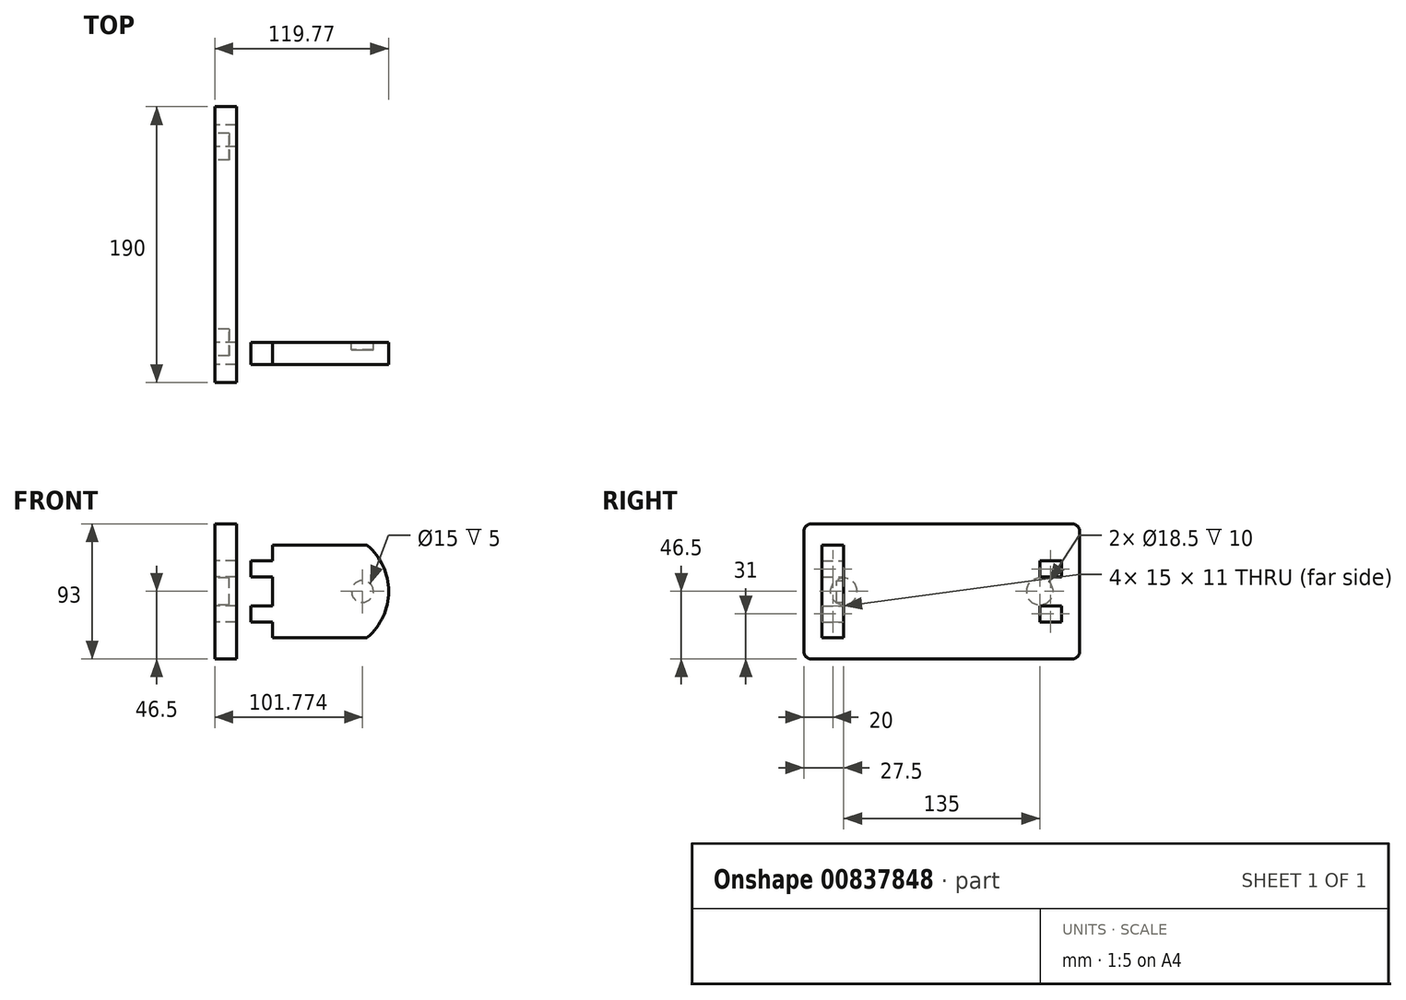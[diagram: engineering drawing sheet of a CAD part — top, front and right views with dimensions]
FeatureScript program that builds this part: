
annotation { "Feature Type Name" : "Feature", "Feature Type Description" : "" }
export const myFeature = defineFeature(function(context is Context, id is Id, definition is map)
    precondition{}
    {
        {
            var Q0;
            Q0=qCreatedBy(makeId("Right.planeOp"),FACE);
            var sketch = newSketch(context, id + "F0", { "sketchPlane" : qUnion([Q0])});
            skLineSegment(sketch, "E0.bottom", {"start": v(90, -46.5) * mm, "end": v(-90, -46.5) * mm});
            skLineSegment(sketch, "E0.top", {"start": v(90, 46.5) * mm, "end": v(-90, 46.5) * mm});
            skLineSegment(sketch, "E0.left", {"start": v(95, -41.5) * mm, "end": v(95, 41.5) * mm});
            skLineSegment(sketch, "E0.right", {"start": v(-95, -41.5) * mm, "end": v(-95, 41.5) * mm});
            skPoint(sketch, "E0.middle", {"position": v(0, 0) * mm});
            skLineSegment(sketch, "E1.bottom", {"start": v(67.5, 21) * mm, "end": v(82.5, 21) * mm});
            skLineSegment(sketch, "E1.top", {"start": v(67.5, 10) * mm, "end": v(82.5, 10) * mm});
            skLineSegment(sketch, "E1.left", {"start": v(67.5, 21) * mm, "end": v(67.5, 10) * mm});
            skLineSegment(sketch, "E1.right", {"start": v(82.5, 21) * mm, "end": v(82.5, 10) * mm});
            skLineSegment(sketch, "E2.bottom", {"start": v(67.5, -10) * mm, "end": v(82.5, -10) * mm});
            skLineSegment(sketch, "E2.top", {"start": v(67.5, -21) * mm, "end": v(82.5, -21) * mm});
            skLineSegment(sketch, "E2.left", {"start": v(67.5, -10) * mm, "end": v(67.5, -21) * mm});
            skLineSegment(sketch, "E2.right", {"start": v(82.5, -10) * mm, "end": v(82.5, -21) * mm});
            skLineSegment(sketch, "E3.bottom", {"start": v(-67.5, -10) * mm, "end": v(-82.5, -10) * mm});
            skLineSegment(sketch, "E3.top", {"start": v(-67.5, -21) * mm, "end": v(-82.5, -21) * mm});
            skLineSegment(sketch, "E3.left", {"start": v(-67.5, -10) * mm, "end": v(-67.5, -21) * mm});
            skLineSegment(sketch, "E3.right", {"start": v(-82.5, -10) * mm, "end": v(-82.5, -21) * mm});
            skLineSegment(sketch, "E4.bottom", {"start": v(-67.5, 10) * mm, "end": v(-82.5, 10) * mm});
            skLineSegment(sketch, "E4.top", {"start": v(-67.5, 21) * mm, "end": v(-82.5, 21) * mm});
            skLineSegment(sketch, "E4.left", {"start": v(-67.5, 10) * mm, "end": v(-67.5, 21) * mm});
            skLineSegment(sketch, "E4.right", {"start": v(-82.5, 10) * mm, "end": v(-82.5, 21) * mm});
            skPoint(sketch, "E5.visualSharp", {"position": v(-95, 46.5) * mm});
            skArc(sketch, "E5.filletArc", {"start": v(-90, 46.5) * mm, "mid": v(-93.54, 45.04) * mm, "end": v(-95, 41.5) * mm});
            skPoint(sketch, "E6.visualSharp", {"position": v(95, 46.5) * mm});
            skArc(sketch, "E6.filletArc", {"start": v(95, 41.5) * mm, "mid": v(93.54, 45.04) * mm, "end": v(90, 46.5) * mm});
            skPoint(sketch, "E7.visualSharp", {"position": v(95, -46.5) * mm});
            skArc(sketch, "E7.filletArc", {"start": v(90, -46.5) * mm, "mid": v(93.54, -45.04) * mm, "end": v(95, -41.5) * mm});
            skPoint(sketch, "E8.visualSharp", {"position": v(-95, -46.5) * mm});
            skArc(sketch, "E8.filletArc", {"start": v(-95, -41.5) * mm, "mid": v(-93.54, -45.04) * mm, "end": v(-90, -46.5) * mm});
            skCircle(sketch, "E9", {"center": v(-67.5, 0) * mm, "radius": 9.25 * mm});
            skCircle(sketch, "E10", {"center": v(67.5, 0) * mm, "radius": 9.25 * mm});
            skSolve(sketch);
        }
        {
            var Q0;
            Q0=makeQuery(id+"F0.imprint","IMPRINT",FACE,{"disambiguationData":[TD([[makeQuery(id+"F0.imprint","IMPRINT",EDGE,{"derivedFrom":sQuery(id+"F0.wireOp",EDGE,"E0.bottom")}),-1.0]])]});
            var Q1;
            {var subQ5=sQuery(id+"F0.wireOp",EDGE,"E1.left");var subQ6=sQuery(id+"F0.wireOp",EDGE,"E1.top");var subQ7=makeQuery(id+"F0.imprint","INTERSECT",VERTEX,{"derivedFrom":[subQ6,subQ5]});Q1=makeQuery(id+"F0.imprint","IMPRINT",FACE,{"disambiguationData":[TD([[makeQuery(id+"F0.imprint","IMPRINT",EDGE,{"disambiguationData":[TD([[subQ7,-1.0]])],"derivedFrom":subQ6}),-1.0]])]});}
            var Q2;
            {var subQ6=sQuery(id+"F0.wireOp",EDGE,"E3.bottom");var subQ8=sQuery(id+"F0.wireOp",EDGE,"E3.left");var subQ9=makeQuery(id+"F0.imprint","INTERSECT",VERTEX,{"derivedFrom":[subQ6,subQ8]});Q2=makeQuery(id+"F0.imprint","IMPRINT",FACE,{"disambiguationData":[TD([[makeQuery(id+"F0.imprint","IMPRINT",EDGE,{"disambiguationData":[TD([[subQ9,-1.0]])],"derivedFrom":subQ6}),-1.0]])]});}
            var Q3;
            Q3=makeQuery(id+"F0.imprint","IMPRINT",FACE,{"disambiguationData":[TD([[makeQuery(id+"F0.imprint","IMPRINT",EDGE,{"derivedFrom":sQuery(id+"F0.wireOp",EDGE,"E9")}),1.0]])]});
            var Q4;
            Q4=makeQuery(id+"F0.imprint","IMPRINT",FACE,{"disambiguationData":[TD([[makeQuery(id+"F0.imprint","IMPRINT",EDGE,{"derivedFrom":sQuery(id+"F0.wireOp",EDGE,"E10")}),1.0]])]});
            extrude(context, id + "F1", {"entities" : qUnion([Q0, Q1, Q2, Q3, Q4]), "depth" : 15 * mm, "offsetDistance" : 25 * mm});
        }
        {
            var Q0;
            Q0=qCreatedBy(makeId("Front.planeOp"),FACE);
            cPlane(context, id + "F2", {"entities" : qUnion([Q0]), "cplaneType" : CPlaneType.OFFSET, "offset" : 67.5 * mm, "width" : 150 * mm, "height" : 150 * mm});
        }
        {
            var Q0;
            Q0=qCreatedBy(id+"F2.planeOp",FACE);
            var sketch = newSketch(context, id + "F3", { "sketchPlane" : qUnion([Q0])});
            skLineSegment(sketch, "E11", {"start": v(104.04, 32) * mm, "end": v(39.77, 32) * mm});
            skLineSegment(sketch, "E12", {"start": v(39.77, 32) * mm, "end": v(39.77, 21) * mm});
            skLineSegment(sketch, "E13", {"start": v(39.77, 21) * mm, "end": v(24.77, 21) * mm});
            skLineSegment(sketch, "E14", {"start": v(24.77, 21) * mm, "end": v(24.77, 10) * mm});
            skLineSegment(sketch, "E15", {"start": v(24.77, 10) * mm, "end": v(39.77, 10) * mm});
            skLineSegment(sketch, "E16", {"start": v(39.77, 10) * mm, "end": v(39.77, -10) * mm});
            skLineSegment(sketch, "E17", {"start": v(39.77, -10) * mm, "end": v(24.77, -10) * mm});
            skLineSegment(sketch, "E18", {"start": v(24.77, -10) * mm, "end": v(24.77, -21) * mm});
            skLineSegment(sketch, "E19", {"start": v(24.77, -21) * mm, "end": v(39.77, -21) * mm});
            skLineSegment(sketch, "E20", {"start": v(39.77, -21) * mm, "end": v(39.77, -32) * mm});
            skLineSegment(sketch, "E21", {"start": v(39.77, -32) * mm, "end": v(104.04, -32) * mm});
            skPoint(sketch, "E22", {"position": v(119.77, 0) * mm});
            skArc(sketch, "E23", {"start": v(105.35, -31.51) * mm, "mid": v(119.77, 0) * mm, "end": v(105.35, 31.51) * mm});
            skPoint(sketch, "E24.visualSharp", {"position": v(104.77, 32) * mm});
            skArc(sketch, "E24.filletArc", {"start": v(105.35, 31.51) * mm, "mid": v(104.74, 31.87) * mm, "end": v(104.04, 32) * mm});
            skPoint(sketch, "E25.visualSharp", {"position": v(104.77, -32) * mm});
            skArc(sketch, "E25.filletArc", {"start": v(104.04, -32) * mm, "mid": v(104.74, -31.87) * mm, "end": v(105.35, -31.51) * mm});
            skCircle(sketch, "E26", {"center": v(101.77, 0) * mm, "radius": 7.5 * mm});
            skSolve(sketch);
        }
        {
            var Q0;
            Q0=makeQuery(id+"F3.imprint","IMPRINT",FACE,{"disambiguationData":[TD([[makeQuery(id+"F3.imprint","IMPRINT",EDGE,{"derivedFrom":sQuery(id+"F3.wireOp",EDGE,"E11")}),1.0]])]});
            var Q1;
            Q1=makeQuery(id+"F3.imprint","IMPRINT",FACE,{"disambiguationData":[TD([[makeQuery(id+"F3.imprint","IMPRINT",EDGE,{"derivedFrom":sQuery(id+"F3.wireOp",EDGE,"E26")}),1.0]])]});
            extrude(context, id + "F4", {"entities" : qUnion([Q0, Q1]), "depth" : 15 * mm, "offsetDistance" : 25 * mm});
        }
        {
            var Q0;
            Q0=makeQuery(id+"F3.imprint","IMPRINT",FACE,{"disambiguationData":[TD([[makeQuery(id+"F3.imprint","IMPRINT",EDGE,{"derivedFrom":sQuery(id+"F3.wireOp",EDGE,"E26")}),1.0]])]});
            extrude(context, id + "F5", {"entities" : qUnion([Q0]), "operationType" : NewBodyOperationType.REMOVE, "depth" : 5 * mm, "offsetDistance" : 25 * mm});
        }
        {
            var Q0;
            Q0=makeQuery(id+"F0.imprint","IMPRINT",FACE,{"disambiguationData":[TD([[makeQuery(id+"F0.imprint","IMPRINT",EDGE,{"derivedFrom":sQuery(id+"F0.wireOp",EDGE,"E10")}),1.0]])]});
            var Q1;
            Q1=makeQuery(id+"F0.imprint","IMPRINT",FACE,{"disambiguationData":[TD([[makeQuery(id+"F0.imprint","IMPRINT",EDGE,{"derivedFrom":sQuery(id+"F0.wireOp",EDGE,"E9")}),1.0]])]});
            extrude(context, id + "F6", {"entities" : qUnion([Q0, Q1]), "operationType" : NewBodyOperationType.REMOVE, "depth" : 10 * mm, "offsetDistance" : 25 * mm});
        }
    });
